# Revit family: RN 80034 Optipress-Aquaplus-Übergang
name_source: partatom
category: Rohrformteile
units: mm (PartAtom-declared; Revit-internal decimal feet)

## family parameters
Arbeitsebenenbasiert = Nein
Beim Laden mit Abzugskörper schneiden = Nein
Bemaßung runder Anschluss = Durchmesser verwenden
Gemeinsam genutzt = Nein
Immer vertikal = Ja
Teiletyp = Verbindung

## types (10) — shared parameters
1.010.00.2 Blattnummer der Richtlinie = 29
1.010.00.3 Ausgabedatum (Monat) der Richtlinie = 201308
1.010.00.4 Herstellername = R. Nussbaum AG
1.010.00.5 Revisionsdatum der Datei = 20190521
1.010.00.6 Webadresse des Herstellers = http://www.nussbaum.ch
1.100.00.4 Produktbezeichnung = Versorgung
1.110.00.2 Index = 4
1.110.00.4 Produktbezeichnung = Optipress
1.960/3L.00.8 Link (URL) = https://www.nussbaum.ch
29.700.00.4 Produktname = Optipress-Aquaplus-Übergang, mit Einsteckende und Innengewinde
29.700.00.5 Produktkennung = 2
29.700.00.6 Querschnittsform = 1
29.700.00.7 Nennweitensystem = DN
29.700.00.8 Nenndrucksystem = PN
29.710.02.4 Nenndruck = 16
29.710.02.5 max. zul. Überdruck [hPa] = 1600
29.710.02.7 max. zul. Dauer-Betriebsdruck [hPa] = 1600
29.710.02.9 max. zul. Dauer-Betriebstemperatur [°C] = 95
Connector Visibility = Nein
EnclosingSpace Visibility = Nein

## per-type parameters (varying)
| type | 1.800.00.3 TGA-Nummer | 1.810.00.3 Hersteller-Bestellnummer | 1.810.00.4 DATANORM-Nummer | 1.810.00.5 StLB-Nummer | 1.810.00.6 GTIN-Nummer | 29.710.02.10 Formstück-Gewicht [kg] | 29.710.02.3 Benennung | CONNECTOR0_DIAMETER_dX_0r | CONNECTOR0_dX_01 | CONNECTOR0_ref_dX | CONNECTOR1_DIAMETER_dX_0r | CONNECTOR1_dX_00 | CONNECTOR1_dX_01 | CONNECTOR1_ref_dX | R. Nussbaum AG 80034.21 de Visibility | R. Nussbaum AG 80034.22 de Visibility | R. Nussbaum AG 80034.23 de Visibility | R. Nussbaum AG 80034.24 de Visibility | R. Nussbaum AG 80034.25 de Visibility | R. Nussbaum AG 80034.28 de Visibility | R. Nussbaum AG 80034.29 de Visibility | R. Nussbaum AG 80034.31 de Visibility | R. Nussbaum AG 80034.33 de Visibility | R. Nussbaum AG 80034.35 de Visibility |
| 80034.21, Optipress-Aquaplus-Übergang, mit Einsteckende und Innengewinde, DN=12x15, L=47, Rp=½ | 01900400000000000000000000000000000000000000000023000000000000000001 | 80034.21 | 80034.21 | 267.232 | 7612945051561 | 0.043 | Optipress-Aquaplus-Übergang, mit Einsteckende und Innengewinde, DN=12x15, L=47, Rp=½ | 12 mm  [stored 0.0393701 ft] | 22 mm | 22 mm | 15 mm | 34 mm | 47 mm | 34 mm | Ja | Nein | Nein | Nein | Nein | Nein | Nein | Nein | Nein | Nein |
| 80034.22, Optipress-Aquaplus-Übergang, mit Einsteckende und Innengewinde, DN=15, L=46, Rp=½ | 01900400000000000000000000000000000000000000000023000000000000000002 | 80034.22 | 80034.22 | 267.233 | 7612945051578 | 0.049 | Optipress-Aquaplus-Übergang, mit Einsteckende und Innengewinde, DN=15, L=46, Rp=½ | 15 mm | 22 mm | 22 mm | 15 mm | 33 mm  [stored 0.108268 ft] | 46 mm | 33 mm  [stored 0.108268 ft] | Nein | Ja | Nein | Nein | Nein | Nein | Nein | Nein | Nein | Nein |
| 80034.23, Optipress-Aquaplus-Übergang, mit Einsteckende und Innengewinde, DN=15, L=51, Rp=¾ | 01900400000000000000000000000000000000000000000023000000000000000003 | 80034.23 | 80034.23 |  | 7612945051585 | 0.073 | Optipress-Aquaplus-Übergang, mit Einsteckende und Innengewinde, DN=15, L=51, Rp=¾ | 15 mm | 22 mm | 22 mm | 20 mm | 36 mm | 51 mm | 36 mm | Nein | Nein | Ja | Nein | Nein | Nein | Nein | Nein | Nein | Nein |
| 80034.24, Optipress-Aquaplus-Übergang, mit Einsteckende und Innengewinde, DN=20x15, L=46, Rp=½ | 01900400000000000000000000000000000000000000000023000000000000000004 | 80034.24 | 80034.24 |  | 7612945051592 | 0.045 | Optipress-Aquaplus-Übergang, mit Einsteckende und Innengewinde, DN=20x15, L=46, Rp=½ | 20 mm | 24 mm | 24 mm | 15 mm | 33 mm  [stored 0.108268 ft] | 46 mm | 33 mm  [stored 0.108268 ft] | Nein | Nein | Nein | Ja | Nein | Nein | Nein | Nein | Nein | Nein |
| 80034.25, Optipress-Aquaplus-Übergang, mit Einsteckende und Innengewinde, DN=20, L=50, Rp=¾ | 01900400000000000000000000000000000000000000000023000000000000000005 | 80034.25 | 80034.25 | 267.234 | 7612945051608 | 0.066 | Optipress-Aquaplus-Übergang, mit Einsteckende und Innengewinde, DN=20, L=50, Rp=¾ | 20 mm | 24 mm | 24 mm | 20 mm | 35 mm | 50 mm  [stored 0.164042 ft] | 35 mm | Nein | Nein | Nein | Nein | Ja | Nein | Nein | Nein | Nein | Nein |
| 80034.28, Optipress-Aquaplus-Übergang, mit Einsteckende und Innengewinde, DN=25x20, L=47, Rp=¾ | 01900400000000000000000000000000000000000000000023000000000000000006 | 80034.28 | 80034.28 |  | 7612945051615 | 0.061 | Optipress-Aquaplus-Übergang, mit Einsteckende und Innengewinde, DN=25x20, L=47, Rp=¾ | 25 mm  [stored 0.082021 ft] | 24 mm | 24 mm | 20 mm | 32 mm | 47 mm | 32 mm | Nein | Nein | Nein | Nein | Nein | Ja | Nein | Nein | Nein | Nein |
| 80034.29, Optipress-Aquaplus-Übergang, mit Einsteckende und Innengewinde, DN=25, L=53, Rp=1 | 01900400000000000000000000000000000000000000000023000000000000000007 | 80034.29 | 80034.29 | 267.235 | 7612945051622 | 0.088 | Optipress-Aquaplus-Übergang, mit Einsteckende und Innengewinde, DN=25, L=53, Rp=1 | 25 mm  [stored 0.082021 ft] | 24 mm | 24 mm | 25 mm  [stored 0.082021 ft] | 36 mm | 53 mm | 36 mm | Nein | Nein | Nein | Nein | Nein | Nein | Ja | Nein | Nein | Nein |
| 80034.31, Optipress-Aquaplus-Übergang, mit Einsteckende und Innengewinde, DN=32, L=59, Rp=1¼ | 01900400000000000000000000000000000000000000000023000000000000000008 | 80034.31 | 80034.31 | 267.236 | 7612945051639 | 0.149 | Optipress-Aquaplus-Übergang, mit Einsteckende und Innengewinde, DN=32, L=59, Rp=1¼ | 32 mm | 26 mm | 26 mm | 32 mm | 40 mm | 59 mm | 40 mm | Nein | Nein | Nein | Nein | Nein | Nein | Nein | Ja | Nein | Nein |
| 80034.33, Optipress-Aquaplus-Übergang, mit Einsteckende und Innengewinde, DN=40, L=73, Rp=1½ | 01900400000000000000000000000000000000000000000023000000000000000009 | 80034.33 | 80034.33 | 267.237 | 7612945051646 | 0.229 | Optipress-Aquaplus-Übergang, mit Einsteckende und Innengewinde, DN=40, L=73, Rp=1½ | 40 mm | 36 mm | 36 mm | 40 mm | 54 mm | 73 mm | 54 mm | Nein | Nein | Nein | Nein | Nein | Nein | Nein | Nein | Ja | Nein |
| 80034.35, Optipress-Aquaplus-Übergang, mit Einsteckende und Innengewinde, DN=50, L=80, Rp=2 | 01900400000000000000000000000000000000000000000023000000000000000010 | 80034.35 | 80034.35 | 267.238 | 7612945051653 | 0.37 | Optipress-Aquaplus-Übergang, mit Einsteckende und Innengewinde, DN=50, L=80, Rp=2 | 50 mm  [stored 0.164042 ft] | 40 mm | 40 mm | 50 mm  [stored 0.164042 ft] | 56 mm | 80 mm | 56 mm | Nein | Nein | Nein | Nein | Nein | Nein | Nein | Nein | Nein | Ja |

note: column(s) folded — value = type name in every type: 1.800.00.4 Kommentarfeld

note: [stored X ft] marks values corroborated as IEEE doubles in the binary element streams (Revit-internal decimal feet)

## geometry (parser evidence)
native form markers: Sweep x2
no freeform markers — native parametric forms only
